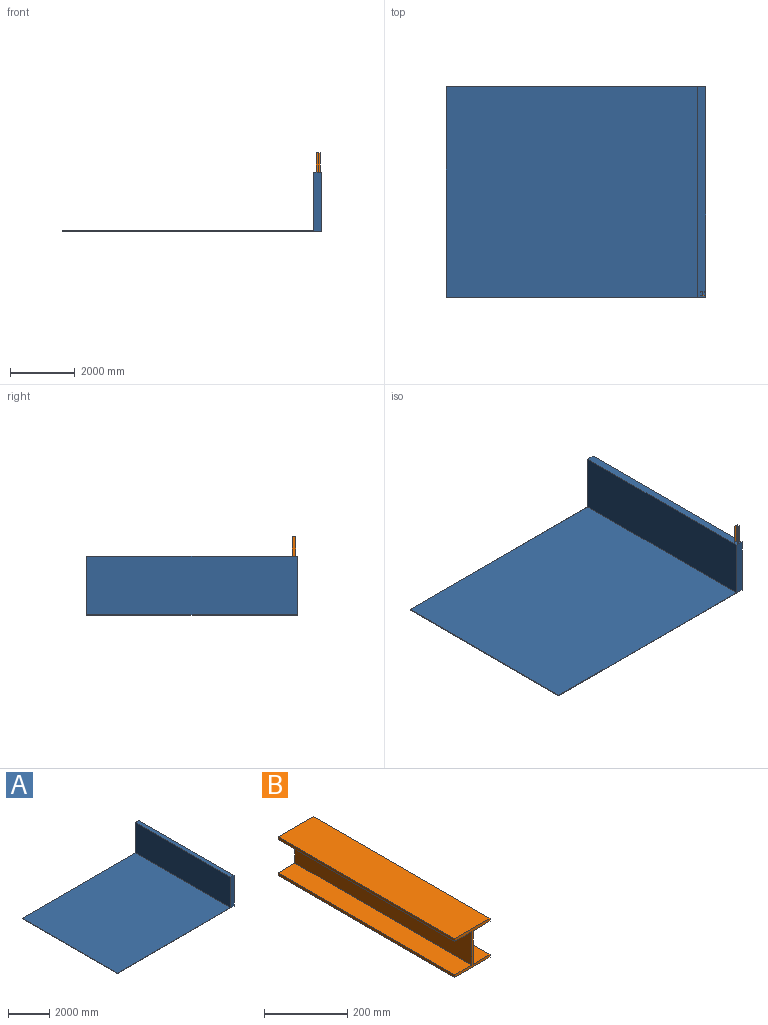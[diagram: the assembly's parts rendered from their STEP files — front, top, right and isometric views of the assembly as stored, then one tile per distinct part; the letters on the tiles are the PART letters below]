
ASSEMBLY  parts=2 mates=1
PART A: 8 faces, bbox 8000x6500x1825 mm
  f0: plane 7760x6500mm, normal (0,0,1), area 50440000mm2, adj f2,f3,f4,f6
  f1: plane 6500x1825mm, normal (1,0,0), area 11862500mm2, adj f2,f4,f5,f7
  f2: plane 8000x1825mm, normal (0,1,0), area 632000mm2, adj f0,f1,f3,f5,f6,f7
  f3: plane 6500x25mm, normal (-1,0,0), area 162500mm2, adj f0,f2,f4,f5
  f4: plane 8000x1825mm, normal (0,-1,0), area 632000mm2, adj f0,f1,f3,f5,f6,f7
  f5: plane 8000x6500mm, normal (0,0,-1), area 52000000mm2, adj f1,f2,f3,f4
  f6: plane 6500x1800mm, normal (-1,0,0), area 11700000mm2, adj f0,f2,f4,f7
  f7: plane 6500x240mm, normal (0,0,1), area 1560000mm2, adj f1,f2,f4,f6
PART B: 14 faces, bbox 120x600x114 mm
  f0: plane 600x57.5mm, normal (0,0,-1), area 34500mm2, adj f1,f11,f12,f13
  f1: plane 600x98mm, normal (-1,0,0), area 58800mm2, adj f0,f2,f12,f13
  f2: plane 600x57.5mm, normal (0,0,1), area 34500mm2, adj f1,f3,f12,f13
  f3: plane 600x8mm, normal (-1,0,0), area 4800mm2, adj f2,f4,f12,f13
  f4: plane 600x120mm, normal (0,0,-1), area 72000mm2, adj f3,f5,f12,f13
  f5: plane 600x8mm, normal (1,0,0), area 4800mm2, adj f4,f6,f12,f13
  f6: plane 600x57.5mm, normal (0,0,1), area 34500mm2, adj f5,f7,f12,f13
  f7: plane 600x98mm, normal (1,0,0), area 58800mm2, adj f6,f8,f12,f13
  f8: plane 600x57.5mm, normal (0,0,-1), area 34500mm2, adj f7,f9,f12,f13
  f9: plane 600x8mm, normal (1,0,0), area 4800mm2, adj f8,f10,f12,f13
  f10: plane 600x120mm, normal (0,0,1), area 72000mm2, adj f9,f11,f12,f13
  f11: plane 600x8mm, normal (-1,0,0), area 4800mm2, adj f0,f10,f12,f13
  f12: plane 120x114mm, normal (0,-1,0), area 2410mm2, adj f0,f1,f2,f3,f4,f5,f6,f7
  f13: plane 120x114mm, normal (0,1,0), area 2410mm2, adj f0,f1,f2,f3,f4,f5,f6,f7
PLACE A t=(-30.95,-1.77,-3792.5)mm
PLACE B rot(axis=(1,0,0),90deg) t=(3867.79,-3147.49,-1392.5)mm
MATE planar B.f12 <-> A.f7  axis (0,0,-1) through (3867.79,-3147.49,-1992.5)mm
